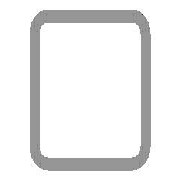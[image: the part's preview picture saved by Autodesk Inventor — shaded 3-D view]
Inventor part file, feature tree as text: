
AUTODESK INVENTOR PART (.ipt)
format: ipt  version: 2025 (Build 290162010, 162A)  size: 131,072 bytes
history: native  units: mm (DEFAULTED — no unit token found)
features: other x4, sketch x1, plane x1
ambient origin geometry x8: Origin, YZ Plane, XZ Plane, XY Plane, X Axis, Y Axis, Z Axis, Center Point
bodies: Solid1 (feature_tree), Body (feature_tree)
feature tree (6):
  parser-record x1  (decoder bookkeeping rows leaked as tree rows — omitted from the tree; the rows remain in map.json)
  other  "Driven Length"
  other  "Start Plane"
  other  "End Plane"
  sketch  "Sketch3"  dims[d3=2100.0mm d4=0.0mm d7=4.0mm d9=40.0mm d11=40.0mm d12=2.0mm d13=-0.0mm d14=2100.0mm d15=20.0mm d16=20.0mm d17=90.0deg d18=2100.0mm]
  plane  "Work Plane3"
